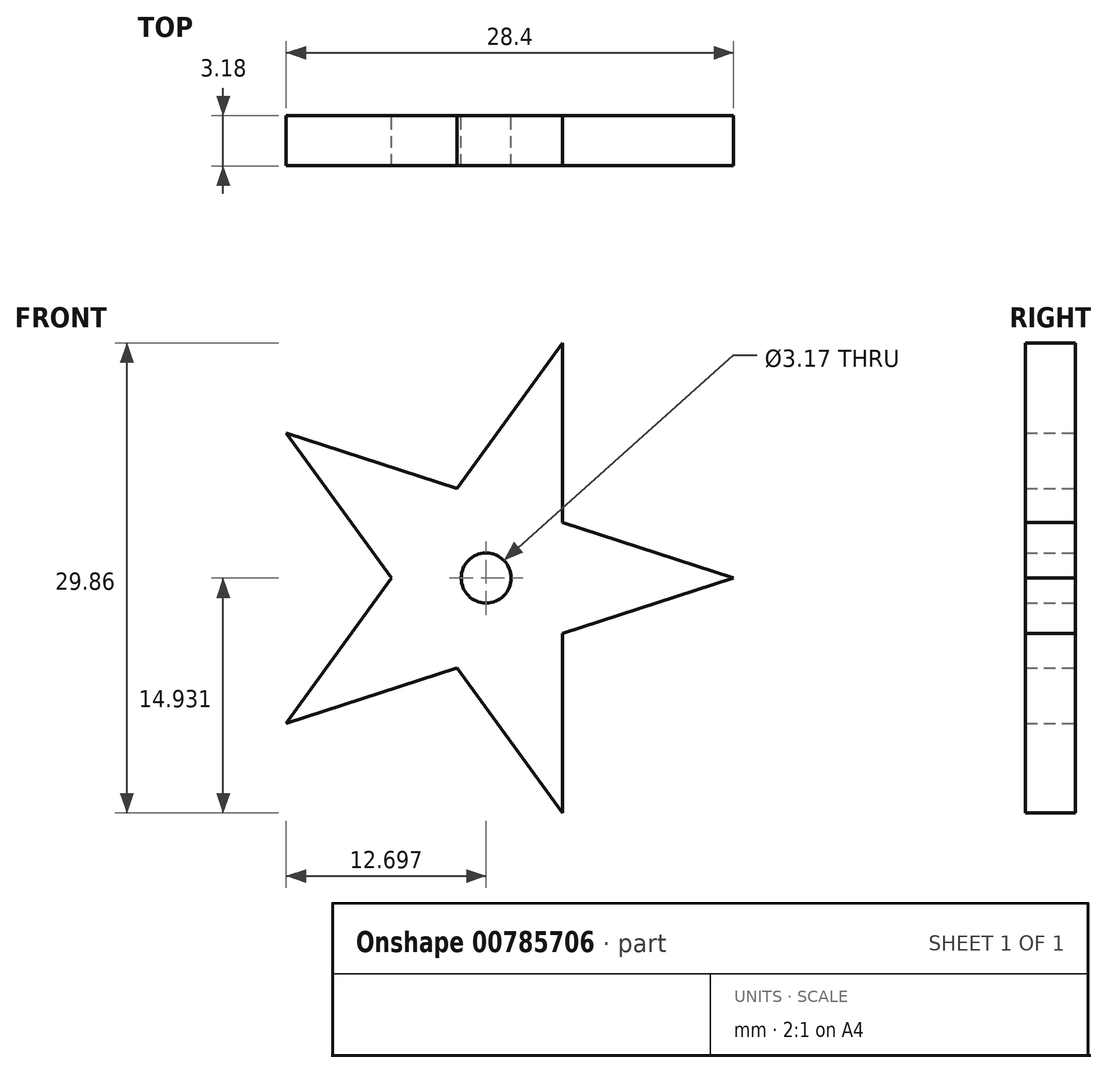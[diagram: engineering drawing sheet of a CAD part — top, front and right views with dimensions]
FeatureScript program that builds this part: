
annotation { "Feature Type Name" : "Feature", "Feature Type Description" : "" }
export const myFeature = defineFeature(function(context is Context, id is Id, definition is map)
    precondition{}
    {
        {
            var Q0;
            Q0=qCreatedBy(makeId("Front.planeOp"),FACE);
            var sketch = newSketch(context, id + "F0", { "sketchPlane" : qUnion([Q0])});
            skArc(sketch, "E0.cCircle", {"start": v(-13.6, 33.55) * mm, "mid": v(-14.2, 32.78) * mm, "end": v(-14.76, 31.96) * mm, "construction": true});
            skPoint(sketch, "E0.0.midPoint", {"position": v(-16.63, 25.31) * mm});
            skLineSegment(sketch, "E1", {"start": v(-16.63, 16.08) * mm, "end": v(-9.93, 25.31) * mm});
            skLineSegment(sketch, "E2", {"start": v(0.92, 10.38) * mm, "end": v(0.92, 21.79) * mm});
            skLineSegment(sketch, "E3", {"start": v(-16.63, 34.54) * mm, "end": v(-5.79, 31.01) * mm});
            skLineSegment(sketch, "E4", {"start": v(-16.63, 16.08) * mm, "end": v(-5.79, 19.6) * mm});
            skLineSegment(sketch, "E5", {"start": v(0.92, 10.38) * mm, "end": v(-5.79, 19.6) * mm});
            skCircle(sketch, "E6", {"center": v(-3.93, 25.31) * mm, "radius": 1.59 * mm});
            skArc(sketch, "E7.trimOffspring", {"start": v(-14.76, 18.67) * mm, "mid": v(-14.2, 17.85) * mm, "end": v(-13.6, 17.07) * mm, "construction": true});
            skArc(sketch, "E8.trimOffspring", {"start": v(-0.96, 12.96) * mm, "mid": v(0, 13.23) * mm, "end": v(0.92, 13.57) * mm, "construction": true});
            skArc(sketch, "E9.trimOffspring", {"start": v(8.73, 24.32) * mm, "mid": v(8.77, 25.31) * mm, "end": v(8.73, 26.3) * mm, "construction": true});
            skArc(sketch, "E10.trimOffspring", {"start": v(0.92, 37.05) * mm, "mid": v(0, 37.39) * mm, "end": v(-0.96, 37.66) * mm, "construction": true});
            skLineSegment(sketch, "E11.trimOffspring", {"start": v(-5.79, 31.01) * mm, "end": v(0.92, 40.24) * mm});
            skLineSegment(sketch, "E12.trimOffspring", {"start": v(0.92, 28.84) * mm, "end": v(11.77, 25.31) * mm});
            skLineSegment(sketch, "E13.trimOffspring", {"start": v(-9.93, 25.31) * mm, "end": v(-16.63, 34.54) * mm});
            skLineSegment(sketch, "E14.trimOffspring", {"start": v(0.92, 21.79) * mm, "end": v(11.77, 25.31) * mm});
            skLineSegment(sketch, "E15.trimOffspring", {"start": v(0.92, 28.84) * mm, "end": v(0.92, 40.24) * mm});
            skSolve(sketch);
        }
        {
            var Q0;
            Q0=makeQuery(id+"F0.imprint","IMPRINT",FACE,{"disambiguationData":[TD([[makeQuery(id+"F0.imprint","IMPRINT",EDGE,{"derivedFrom":sQuery(id+"F0.wireOp",EDGE,"E1")}),-1.0]])]});
            extrude(context, id + "F1", {"entities" : qUnion([Q0]), "depth" : 3.17 * mm, "offsetDistance" : 25.4 * mm});
        }
    });
